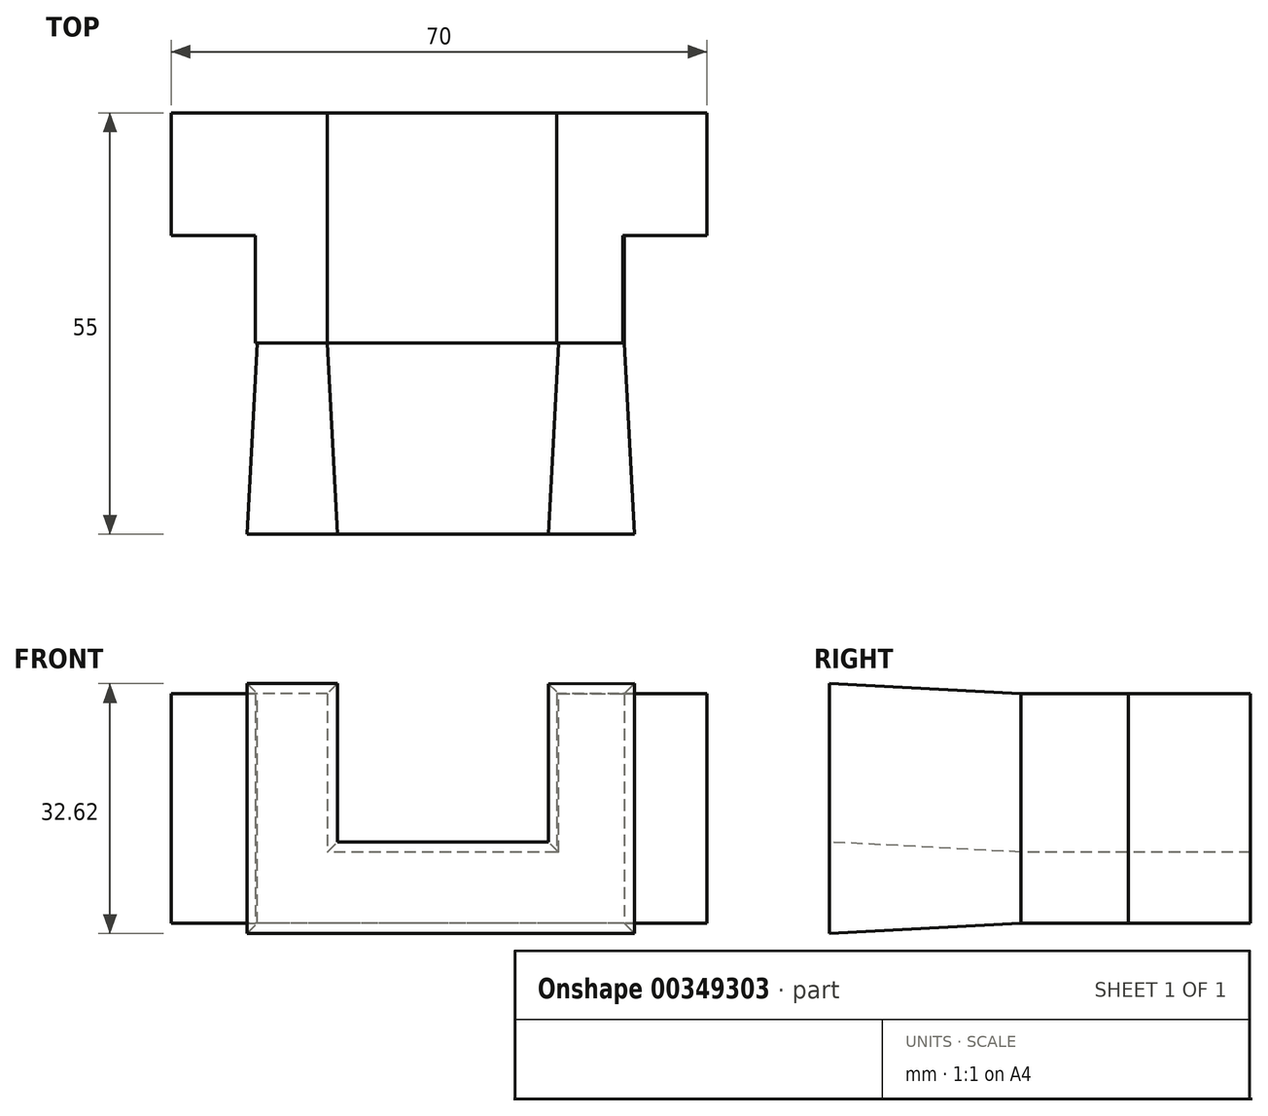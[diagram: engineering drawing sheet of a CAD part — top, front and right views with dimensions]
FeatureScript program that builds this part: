
annotation { "Feature Type Name" : "Feature", "Feature Type Description" : "" }
export const myFeature = defineFeature(function(context is Context, id is Id, definition is map)
    precondition{}
    {
        {
            var Q0;
            Q0=qCreatedBy(makeId("Top.planeOp"),FACE);
            var sketch = newSketch(context, id + "F0", { "sketchPlane" : qUnion([Q0])});
            skLineSegment(sketch, "E0", {"start": v(-19.47, 0) * mm, "end": v(-14.94, 0) * mm});
            skLineSegment(sketch, "E1", {"start": v(23.7, 0) * mm, "end": v(23.7, 14) * mm});
            skLineSegment(sketch, "E2", {"start": v(23.7, 14) * mm, "end": v(34.7, 14) * mm});
            skLineSegment(sketch, "E3", {"start": v(34.7, 14) * mm, "end": v(34.7, 30) * mm});
            skLineSegment(sketch, "E4", {"start": v(34.7, 30) * mm, "end": v(-35.3, 30) * mm});
            skLineSegment(sketch, "E5", {"start": v(-35.3, 30) * mm, "end": v(-35.3, 14) * mm});
            skLineSegment(sketch, "E6", {"start": v(-35.3, 14) * mm, "end": v(-24.3, 14) * mm});
            skLineSegment(sketch, "E7", {"start": v(-24.3, 14) * mm, "end": v(-24.3, 0) * mm});
            skLineSegment(sketch, "E8", {"start": v(-19.47, 0) * mm, "end": v(-24.3, 0) * mm});
            skLineSegment(sketch, "E9", {"start": v(-14.94, 0) * mm, "end": v(-14.94, 30) * mm});
            skLineSegment(sketch, "E10", {"start": v(15.06, 30) * mm, "end": v(15.06, 0) * mm});
            skLineSegment(sketch, "E11.trimOffspring", {"start": v(15.06, 0) * mm, "end": v(23.7, 0) * mm});
            skSolve(sketch);
        }
        {
            var Q0;
            Q0 = qSketchRegion(id + "F0", true);
            extrude(context, id + "F1", {"entities" : qUnion([Q0]), "depth" : 30 * mm});
        }
        {
            var Q0;
            Q0=qCreatedBy(makeId("Front.planeOp"),FACE);
            var sketch = newSketch(context, id + "F2", { "sketchPlane" : qUnion([Q0])});
            skLineSegment(sketch, "E12", {"start": v(23.91, 0) * mm, "end": v(-24.09, 0) * mm});
            skPoint(sketch, "E13.start.orphan", {"position": v(-24.09, 30) * mm});
            skPoint(sketch, "E14.end.orphan", {"position": v(23.91, 30) * mm});
            skLineSegment(sketch, "E15", {"start": v(-15.8, 9.31) * mm, "end": v(-14.9, 9.31) * mm});
            skLineSegment(sketch, "E16", {"start": v(15.3, 9.31) * mm, "end": v(15.3, 29.99) * mm});
            skLineSegment(sketch, "E17", {"start": v(15.3, 29.99) * mm, "end": v(23.91, 30) * mm});
            skLineSegment(sketch, "E18", {"start": v(-24.09, 30) * mm, "end": v(-14.9, 30) * mm});
            skLineSegment(sketch, "E19", {"start": v(-14.9, 30) * mm, "end": v(-14.9, 9.31) * mm});
            skLineSegment(sketch, "E20", {"start": v(-24.09, 0) * mm, "end": v(-24.09, 30) * mm});
            skLineSegment(sketch, "E21", {"start": v(15.3, 9.31) * mm, "end": v(-14.9, 9.31) * mm});
            skLineSegment(sketch, "E22", {"start": v(23.91, 0) * mm, "end": v(23.91, 30) * mm});
            skSolve(sketch);
        }
        {
            var Q0;
            Q0 = qSketchRegion(id + "F2", true);
            extrude(context, id + "F3", {"entities" : qUnion([Q0]), "oppositeDirection" : true, "depth" : 30 * mm});
        }
        {
            var Q0;
            Q0=makeQuery(id+"F3.opExtrude","CAP_FACE",FACE,{"disambiguationData":[OSD([sQuery(id+"F2.wireOp",EDGE,"E16"),sQuery(id+"F2.wireOp",EDGE,"E17"),sQuery(id+"F2.wireOp",EDGE,"E12"),sQuery(id+"F2.wireOp",EDGE,"E18"),sQuery(id+"F2.wireOp",EDGE,"E19"),sQuery(id+"F2.wireOp",EDGE,"E20"),sQuery(id+"F2.wireOp",EDGE,"E21"),sQuery(id+"F2.wireOp",EDGE,"E22")])],"isStart":true});
            extrude(context, id + "F4", {"entities" : qUnion([Q0]), "operationType" : NewBodyOperationType.ADD, "depth" : 25 * mm, "hasDraft" : true, "draftAngle" : 3 * degree});
        }
    });
